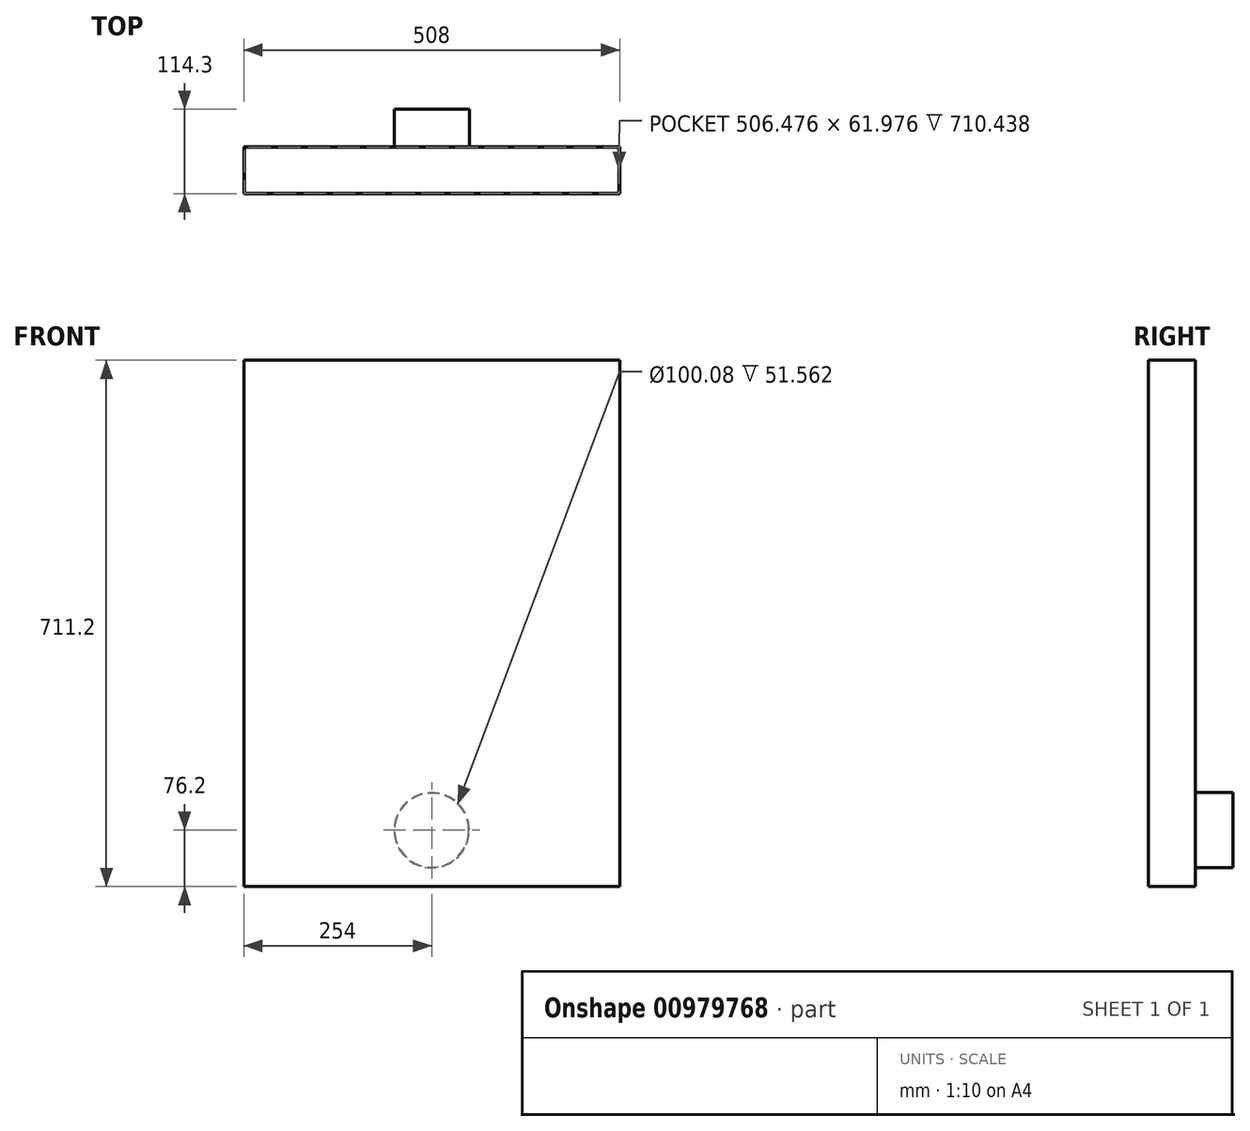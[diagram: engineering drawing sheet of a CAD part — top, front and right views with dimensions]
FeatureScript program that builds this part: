
annotation { "Feature Type Name" : "Feature", "Feature Type Description" : "" }
export const myFeature = defineFeature(function(context is Context, id is Id, definition is map)
    precondition{}
    {
        {
            var Q0;
            Q0=qCreatedBy(makeId("Top.planeOp"),FACE);
            var sketch = newSketch(context, id + "F0", { "sketchPlane" : qUnion([Q0])});
            skLineSegment(sketch, "E0.bottom", {"start": v(-254, 31.75) * mm, "end": v(254, 31.75) * mm});
            skLineSegment(sketch, "E0.top", {"start": v(-254, -31.75) * mm, "end": v(254, -31.75) * mm});
            skLineSegment(sketch, "E0.left", {"start": v(-254, 31.75) * mm, "end": v(-254, -31.75) * mm});
            skLineSegment(sketch, "E0.right", {"start": v(254, 31.75) * mm, "end": v(254, -31.75) * mm});
            skPoint(sketch, "E1", {"position": v(-254, 0) * mm});
            skPoint(sketch, "E2", {"position": v(0, 31.75) * mm});
            skLineSegment(sketch, "E3.bottom", {"start": v(-253.24, 30.99) * mm, "end": v(253.24, 30.99) * mm});
            skLineSegment(sketch, "E3.top", {"start": v(-253.24, -30.99) * mm, "end": v(253.24, -30.99) * mm});
            skLineSegment(sketch, "E3.left", {"start": v(-253.24, 30.99) * mm, "end": v(-253.24, -30.99) * mm});
            skLineSegment(sketch, "E3.right", {"start": v(253.24, 30.99) * mm, "end": v(253.24, -30.99) * mm});
            skSolve(sketch);
        }
        {
            var Q0;
            Q0=makeQuery(id+"F0.imprint","IMPRINT",FACE,{"disambiguationData":[TD([[makeQuery(id+"F0.imprint","IMPRINT",EDGE,{"derivedFrom":sQuery(id+"F0.wireOp",EDGE,"E0.bottom")}),-1.0]])]});
            extrude(context, id + "F1", {"entities" : qUnion([Q0]), "depth" : 711.2 * mm, "offsetDistance" : 25.4 * mm});
        }
        {
            var Q0;
            Q0=makeQuery(id+"F0.imprint","IMPRINT",FACE,{"disambiguationData":[TD([[makeQuery(id+"F0.imprint","IMPRINT",EDGE,{"derivedFrom":sQuery(id+"F0.wireOp",EDGE,"E3.bottom")}),-1.0]])]});
            extrude(context, id + "F2", {"entities" : qUnion([Q0]), "operationType" : NewBodyOperationType.ADD, "depth" : 0.76 * mm, "offsetDistance" : 25.4 * mm});
        }
        {
            var Q0;
            Q0=makeQuery(id+"F1.opExtrude","SWEPT_FACE",FACE,{"disambiguationData":[OSD([sQuery(id+"F0.wireOp",EDGE,"E0.bottom")])]});
            var sketch = newSketch(context, id + "F3", { "sketchPlane" : qUnion([Q0])});
            skCircle(sketch, "E4", {"center": v(0, 76.2) * mm, "radius": 50.8 * mm});
            skCircle(sketch, "E5", {"center": v(0, 76.2) * mm, "radius": 50.04 * mm});
            skSolve(sketch);
        }
        {
            var Q0;
            Q0=makeQuery(id+"F3.imprint","IMPRINT",FACE,{"disambiguationData":[TD([[makeQuery(id+"F3.imprint","IMPRINT",EDGE,{"derivedFrom":sQuery(id+"F3.wireOp",EDGE,"E4")}),1.0]])]});
            extrude(context, id + "F4", {"entities" : qUnion([Q0]), "operationType" : NewBodyOperationType.ADD, "depth" : 50.8 * mm, "offsetDistance" : 25.4 * mm});
        }
        {
            var Q0;
            Q0=makeQuery(id+"F3.imprint","IMPRINT",FACE,{"disambiguationData":[TD([[makeQuery(id+"F3.imprint","IMPRINT",EDGE,{"derivedFrom":sQuery(id+"F3.wireOp",EDGE,"E5")}),1.0]])]});
            extrude(context, id + "F5", {"entities" : qUnion([Q0]), "operationType" : NewBodyOperationType.REMOVE, "oppositeDirection" : true, "depth" : 25.4 * mm, "offsetDistance" : 25.4 * mm});
        }
    });
